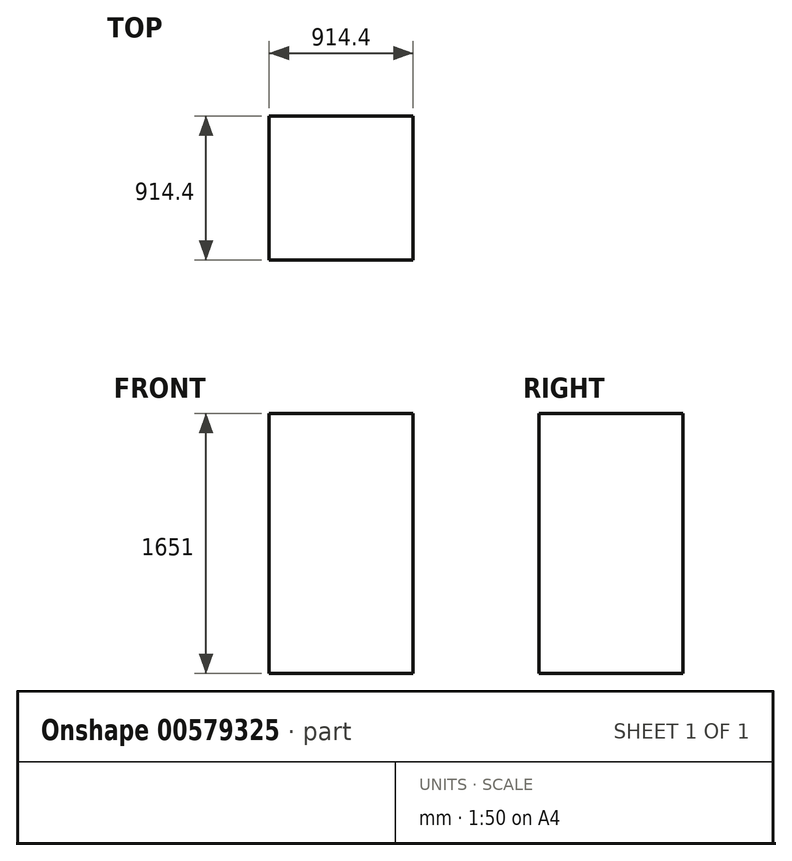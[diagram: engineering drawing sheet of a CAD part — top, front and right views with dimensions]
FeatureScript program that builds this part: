
annotation { "Feature Type Name" : "Feature", "Feature Type Description" : "" }
export const myFeature = defineFeature(function(context is Context, id is Id, definition is map)
    precondition{}
    {
        {
            var Q0;
            Q0=qCreatedBy(makeId("Top.planeOp"),FACE);
            var sketch = newSketch(context, id + "F0", { "sketchPlane" : qUnion([Q0])});
            skPoint(sketch, "E0.middle", {"position": v(0, 0) * mm});
            skLineSegment(sketch, "E1.bottom", {"start": v(-457.2, -457.2) * mm, "end": v(457.2, -457.2) * mm});
            skLineSegment(sketch, "E1.top", {"start": v(-457.2, 457.2) * mm, "end": v(457.2, 457.2) * mm});
            skLineSegment(sketch, "E1.left", {"start": v(-457.2, -457.2) * mm, "end": v(-457.2, 457.2) * mm});
            skLineSegment(sketch, "E1.right", {"start": v(457.2, -457.2) * mm, "end": v(457.2, 457.2) * mm});
            skSolve(sketch);
        }
        {
            var Q0;
            Q0=makeQuery(id+"F0.imprint","IMPRINT",FACE,{"disambiguationData":[TD([[makeQuery(id+"F0.imprint","IMPRINT",EDGE,{"derivedFrom":sQuery(id+"F0.wireOp",EDGE,"E1.bottom")}),1.0]])]});
            extrude(context, id + "F1", {"entities" : qUnion([Q0]), "depth" : 1651 * mm, "offsetDistance" : 25.4 * mm});
        }
    });
